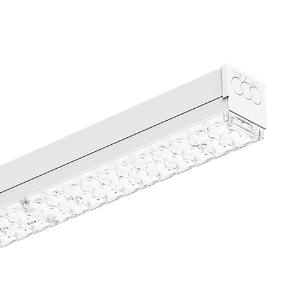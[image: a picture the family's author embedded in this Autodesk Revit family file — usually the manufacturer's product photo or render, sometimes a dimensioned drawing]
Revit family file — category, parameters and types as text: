
# Revit family: 3f_filippi_-_3f_zeta_l_ugr_3f_filippi_-_11028_-_3f_zeta_l_ugr_50_led_dali_l1783
name_source: partatom
category: Lighting Fixtures
units: mm (PartAtom-declared; Revit-internal decimal feet)

## family parameters
Cut with Voids When Loaded = No
Host = Face
Light Source = No
Part Type = Normal
Room Calculation Point = No
Round Connector Dimension = Use Diameter
Shared = No

## types (1)
- 3F Filippi - 3F Zeta L UGR (1 x LED, 8221 lm, 46 W, 4000 K)
    Apparent Load = 46 VA
    Approval mark = ENEC
    CIE Flux Codes = 83 96 99 97 100
    Color Rendering = 80
    Color Temperature = 4000 K
    Control Gear = Electronic transformer
    Default Elevation = 1800 mm
    Description = ILLUMINOTECHNICAL
Luminous efficiency 100% (DLOR 97%, ULOR 3%).
Initial luminous flux of the luminaire 8221 lm.
Controlled direct symmetric distribution.
Installation Interdistance Transv.D = 1.39 x hu - Long.D = 1.30 x hu.
Average luminance <3000 cd/m² for radial angles >65°.
Tabular UGR (CIE 117 - 4H-8H; S=0.25H; 70/50/20): RUG 19.2 - 17.6.
Beam angle: 78° - 75°.
Luminous efficacy 179 lm/W.
Lifetime (L93/B10): 30000 h. (tq+25°C)
Lifetime (L90/B10): 50000 h. (tq+25°C)
Lifetime (L85/B10): 80000 h. (tq+25°C)
Lifetime (L80/B10): 100000 h. (tq+25°C)
Sudden decreased luminous flux after 50000 hours: 0% (C0).
Photobiological safety in compliance with IEC/TR 62778: RG0 risk exempt, (IEC 62471).
In compliance with IEC/EN 62722-2-1 - IEC/EN 62717 standards.

SOURCE
Linear LED module 50W/840.
Energy efficiency class (UE 2019/2020 - UE 2019/2015): C.
CIE 13.3 Colour rendering index: CRI >80 (R9 <50%).
IES TM-30 Fidelity Index: Rf = 84 Rg = 95.
CCT nominal colour temperature 4000 K.
Colour initial tolerance (MacAdam): SDCM 3.

MECHANICAL
Housing in hot-galvanised steel, painted in white polyester, obtained through rolling process.
Light unit in hot-galvanised steel, painted in white polyester base with fixing springs and retractable safety hooks in stainless steel.
Transparent methacrylate (PMMA) controlled distribution lenses with flat external surface.
End caps in white polycarbonate.
Pair of stainless steel sliding brackets with sliding block screws.
Luminaire with limited surface temperature. - D - (EN 60598-2-24)
Dimensions: 1783x62 mm, height 65 mm. Weight 4.01 kg.
IP40 protection degree.
Mechanical strength to impacts IK06 (1 joule).
Glow-wire test resistance 650°C.

ELECTRICAL
Halogen Free DALI-2, PUSH-DIM, electronic wiring 230V-50/60Hz, power factor 0.95 at full load, THD <25%, constant output current, class I, 1 driver, 1 DALI addresse.
Power of the luminaire 46 W.
CE - IEC 60598-1 - EN 60598-1.
SAFE FLICKER: PstLM=<1 and SVM=<0.4 (IEC TR 61547-1 and IEC TR 63158), to ensure a more comfortable and safe light.
Luminaire compliant with EN 60598-2-22 for power supply from a centralised emergency system CPSS (Central Power Supply System), not incorporated in the luminaire - high risk areas excluded. The default power and flux are 100% in AC and 15% in DC.
Ambient temperature from 0°C to +25°C.
Temperature class T6 max 85°C.
Relative humidity UR: <85%.

INSTALLATION
Ceiling / Suspended / Wall.
All accessories dedicated to this product are available on the Catalog and on our website www.3F-Filippi.com.

APPLICATIONS
Suitable product for food production plants (HACCP), IFS (Food Version 6), BRC (GSFS Food Version 7).
In commercial environments, exhibition areas, shops and stores.
In environments with VDTs, managerial offices and staterooms, public offices and schools.

LIGHT MANAGEMENT
Recommended minimum setting: 10%.
The device, equipped with DALI-2 driver, can be controlled manually with 3F Easy Dim technology or automatically/manually with 3F Smart Dimming technology and/or centralised DALI systems.
DALI-2 certification guarantees interoperability with other devices with the same certification.
In electrical systems without a regulation system (manual or automatic) and DALI bus, a suitable jumper must be made on the DA-DA terminals of the appliance.

WARNING
Luminaire designed for disposal/recycling at end-of-life.
Replaceable (LED only) light source by a professional. Replaceable control gear by a professional.
    Height = 65 mm
    Lamp = 1 x LED
    Lamp Light Flux = 8221 lm
    Lamp Power = 46 W
    Lamp count = 1
    Length = 1783 mm
    Lifetime = 50000 h
    Luminous efficacy = 179 lm/W
    Manufacturer = 3F Filippi
    ModVariant = No
    Model = 3F Filippi - 11028 - 3F Zeta L UGR 50 LED DALI L1783
    Mounting Place = Ceiling
    Mounting Type = Pendant
    Number of Poles = 1
    OnlyDefault = Yes
    Power Factor = 1
    Product Name = 3F Filippi - 3F Zeta L UGR
    Product group = pendant luminaire
    ProductGroupID = 9
    Protection Class = Protection class I
    Protection Degree = IP 40
    RLX_Detail_Level = 1
    RLX_Emergency_Light_Flux = 0 lm
    RLX_Emergency_Type = 0
    RLX_Emergency_Type_DB = No
    RlxData = <blob elided: 50269 chars, md5=ad4dc27d>
    Socket = socket
    Standby Power = 0 W
    System Light Flux = 8221 lm
    System Power = 46 W
    Type Comments = Product without accessories
    Type Image = 3ffilippi_3f_zeta_l_ugr.jpg
    URL = http://relux.com
    VarID = ---
    Voltage = 0 V
    Weight = 0.00 kg
    Width = 62 mm  [stored 0.203412 ft]

note: [stored X ft] marks values corroborated as IEEE doubles in the binary element streams (Revit-internal decimal feet)

## geometry (parser evidence)
native form markers: Blend x4, Sweep x10
no freeform markers — native parametric forms only
